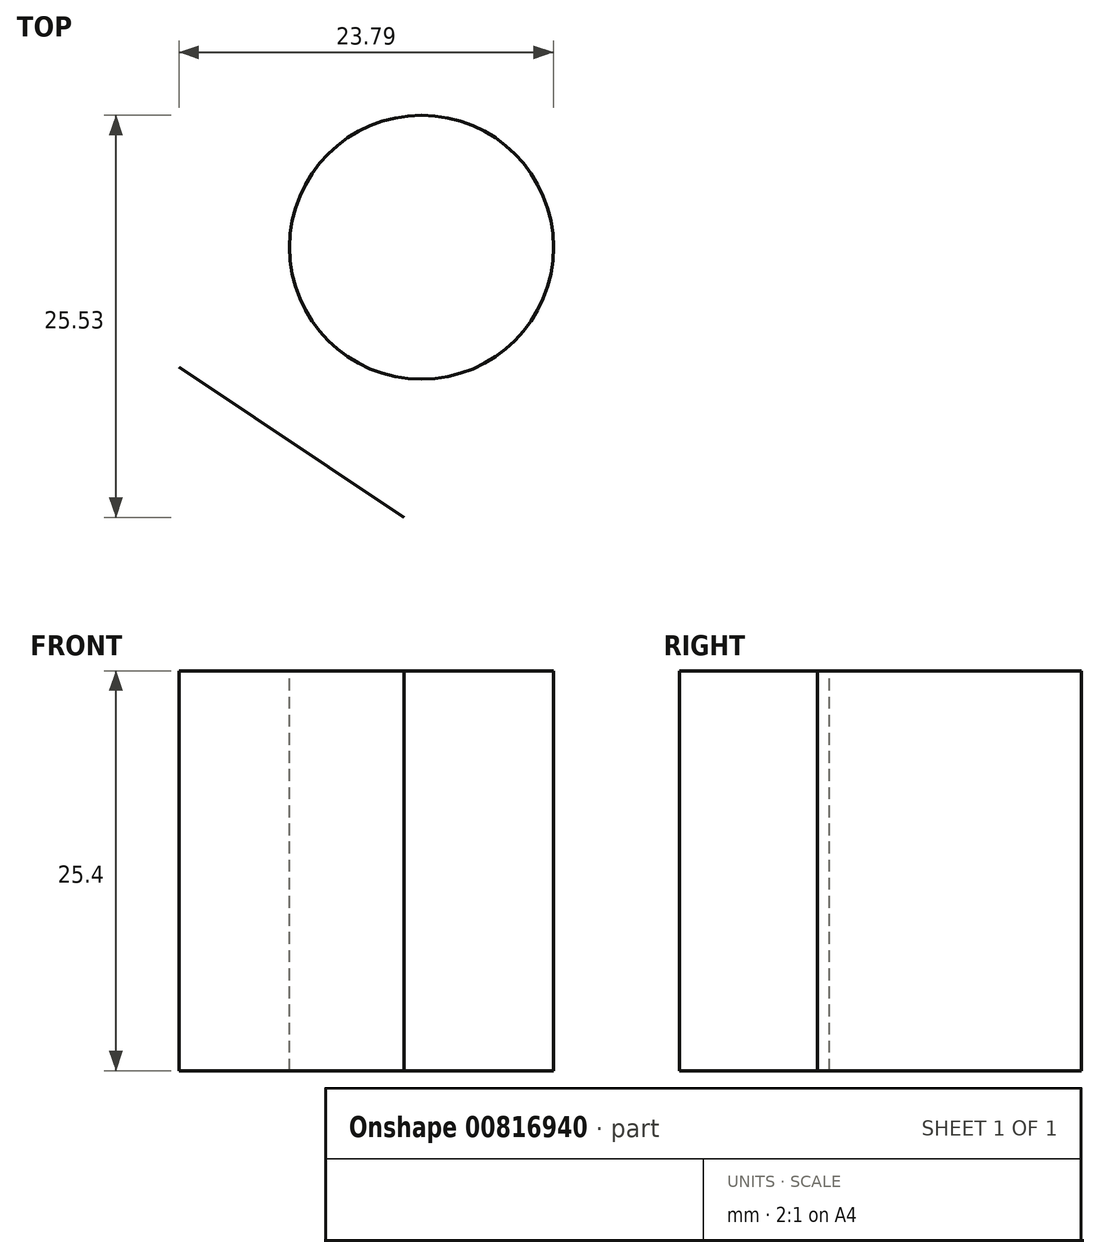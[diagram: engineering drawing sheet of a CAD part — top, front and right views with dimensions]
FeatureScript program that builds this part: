
annotation { "Feature Type Name" : "Feature", "Feature Type Description" : "" }
export const myFeature = defineFeature(function(context is Context, id is Id, definition is map)
    precondition{}
    {
        {
            var Q0;
            Q0=qCreatedBy(makeId("Top.planeOp"),FACE);
            var sketch = newSketch(context, id + "F0", { "sketchPlane" : qUnion([Q0])});
            skCircle(sketch, "E0.cCircle", {"center": v(0, 0) * mm, "radius": 14.89 * mm, "construction": true});
            skLineSegment(sketch, "E0.0", {"start": v(-14.3, 9.54) * mm, "end": v(1.1, 17.15) * mm});
            skLineSegment(sketch, "E0.1", {"start": v(1.1, 17.15) * mm, "end": v(15.4, 7.62) * mm});
            skLineSegment(sketch, "E0.2", {"start": v(15.4, 7.62) * mm, "end": v(14.3, -9.54) * mm});
            skLineSegment(sketch, "E0.3", {"start": v(14.3, -9.54) * mm, "end": v(-1.1, -17.15) * mm});
            skLineSegment(sketch, "E0.4", {"start": v(-1.1, -17.15) * mm, "end": v(-15.4, -7.62) * mm});
            skLineSegment(sketch, "E0.5", {"start": v(-15.4, -7.62) * mm, "end": v(-14.3, 9.54) * mm});
            skPoint(sketch, "E0.0.midPoint", {"position": v(-6.6, 13.34) * mm});
            skCircle(sketch, "E1", {"center": v(0, 0) * mm, "radius": 8.38 * mm});
            skSolve(sketch);
        }
        {
            var Q0;
            Q0=sQuery(id+"F0.wireOp",EDGE,"E1");
            var Q1;
            Q1=sQuery(id+"F0.wireOp",EDGE,"E0.4");
            extrude(context, id + "F1", {"bodyType" : ToolBodyType.SURFACE, "surfaceEntities" : qUnion([Q0, Q1]), "depth" : 25.4 * mm, "offsetDistance" : 25.4 * mm});
        }
    });
